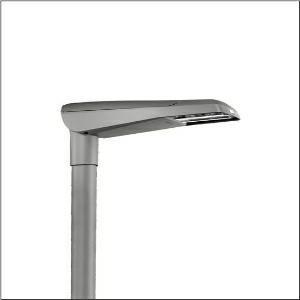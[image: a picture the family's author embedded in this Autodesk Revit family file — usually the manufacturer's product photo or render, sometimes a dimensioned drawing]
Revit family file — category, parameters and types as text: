
# Revit family: streetlight_sl_11_iq_micro___p1_0a_5xc1cc1f08ce_9736
name_source: partatom
category: Lighting Fixtures
units: mm (PartAtom-declared; Revit-internal decimal feet)

## family parameters
Cut with Voids When Loaded = No
Host = Face
Light Source = No
Part Type = Normal
Room Calculation Point = No
Round Connector Dimension = Use Diameter
Shared = No

## types (1)
- --- (1 x LED, 1360 lm, 12.2 W, 2200K)
    Apparent Load = 12 VA
    CIE Flux Codes = 29 63 93 100 100
    Color Rendering = 70
    Color Temperature = 2200K
    Default Elevation = 1800 mm
    Description = Streetlight SL 11 iQ micro, mast luminaire, primary light control with 3 zone facetted reflector, of plastic, silver coated, highly specular, primary optical cover: cover, of PMMA, transparent, light distribution: P1.0a, light emission: direct distribution, primary light characteristic: asymmetric, installation type: post-top, side-entry, lamps: LED, High Power LED, rated values: 1.600lm | 12W | 133,3lm/W (begin service life); end service life: 1.600lm | 12,2W; at 50% lumin. flux: 800lm | 6,7W | 119,4lm/W, colour temperature: 2200/2700/3000/4000K, colour rendering: CRI > 70, light colour: 722/727/730/740, light setting 1 begin service life: 100% | 1.600lm | 12W | 133,3lm/W | 3.000K, light setting 1 end service life: 12,2W, further light settings possible, control: Street-Remote, Auto-Match, Temp-Guard, Lumen-Switch, Night-Set, Smart-Wire, Light-Fading, Desk-Remote (wireless, voltage-free reading and setting of iQ features in the workshop via application-optimized NFC function/RFID function), optimised constant luminous flux control (CLO 2.0), with cable H07RN-F 3x 1.5mm², mains connection: 220..240V, AC, 50/60Hz, connection cable pre-assembled, cable length: 5,5m, luminaire housing, of diecast aluminium, powder-coated, SITECO metallic grey (DB 702S), please order mast flange separately, inclination adjustable without tools: 0°, 5°, 10°, 15° (post-top) | 0°, -5°, -10°, -15° (side-entry), sealing non-destructively replaceable, multi-level sealing system, length: 600mm, width: 174mm, height: 116mm, mast flange for spigot size: 42mm (side-entry): 5XC10008XM4, 60/48mm (side-entry/post-top): 5XC10108XM2, 76/60mm (side-entry/post-top): 5XC10108XM1, equipment: standard, protection rating (complete): IP66, insulation class (complete): insulation class II (safety insulation), certification: CE, ENEC, ENEC+, VDE, impact resistance: IK10, permissible operating ambient temperature for outdoor applications: -25..+50°C, standard-compliant lighting for roads and squares, Environmental Product Declaration (EPD) tested and certified by an independent institute, packaging unit: 1 piece

Light Distribution: P1.0a
    Height = 116 mm
    Lamp = 1 x LED
    Lamp Light Flux = 1360 lm
    Lamp Power = 12.2 W
    Lamp count = 1
    Length = 600 mm
    Luminous efficacy = 111 lm/W
    Manufacturer = Siteco
    ModVariant = No
    Model = 5XC1CC1F08CE
    Number of Poles = 1
    OnlyDefault = Yes
    Power Factor = 1
    Product Name = Streetlight SL 11 iQ micro | P1.0a
    Product group = mast luminaire | pylon top
    ProductGroupID = 6100
    Protection Class = Protection class II
    Protection Degree = IP 66
    RLX_Detail_Level = 1
    RLX_Emergency_Light_Flux = 0 lm
    RLX_Emergency_Type = 0
    RLX_Emergency_Type_DB = No
    RlxData = <blob elided: 58109 chars, md5=590e7d8d>
    Socket = socket
    Standby Power = 0 W
    System Light Flux = 1360 lm
    System Power = 12 W
    Type Comments = individual setting: luminous flux: 100 % | dim-lin: 254 | 318 mA
    Type Image = l_1006566.jpg
    URL = http://relux.com
    VarID = @adj_042301
    Voltage = 0 V
    Weight = 0.00 kg
    Width = 174 mm

## geometry (parser evidence)
native form markers: Blend x4, Sweep x11
no freeform markers — native parametric forms only
